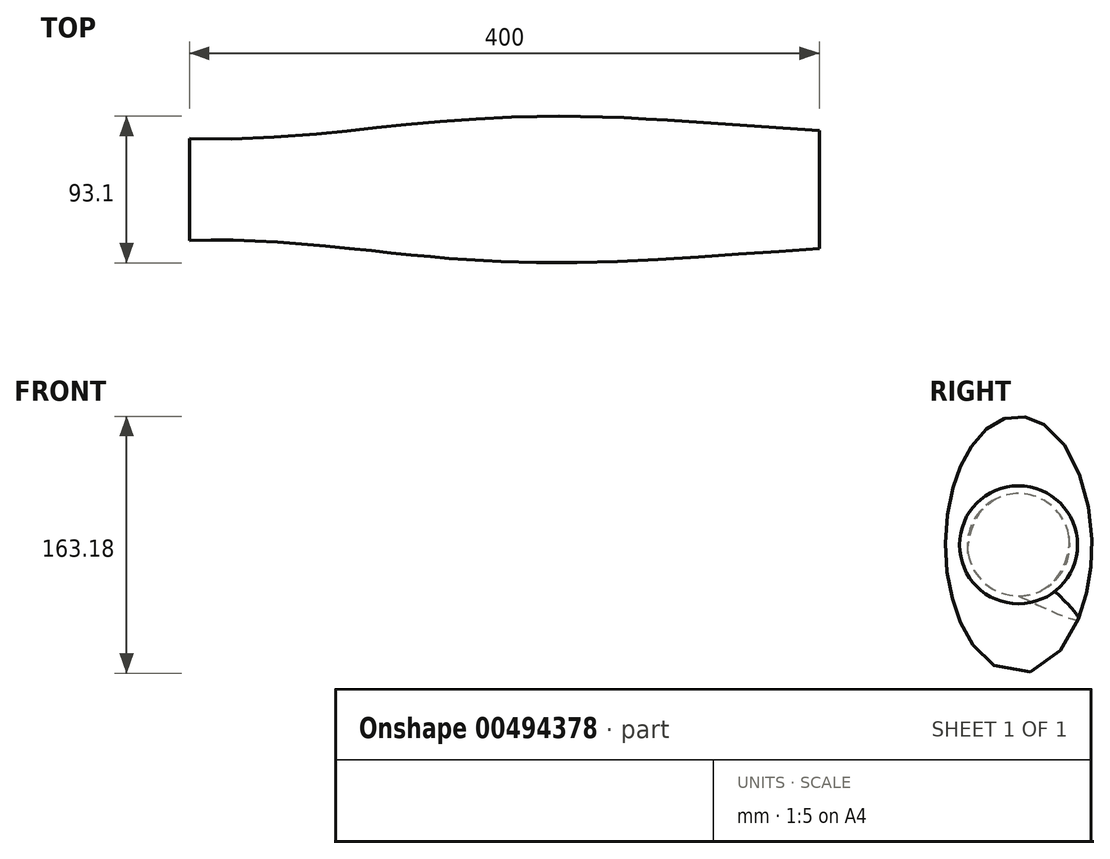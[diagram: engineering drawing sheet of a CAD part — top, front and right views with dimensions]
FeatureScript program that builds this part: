
annotation { "Feature Type Name" : "Feature", "Feature Type Description" : "" }
export const myFeature = defineFeature(function(context is Context, id is Id, definition is map)
    precondition{}
    {
        {
            var Q0;
            Q0=qCreatedBy(makeId("Right.planeOp"),FACE);
            var sketch = newSketch(context, id + "F0", { "sketchPlane" : qUnion([Q0])});
            skEllipse(sketch, "E0", {"center": v(0, 0) * mm, "majorRadius": 45.89 * mm, "minorRadius": 81.4 * mm, "majorAxis": v(1, 0)});
            skSolve(sketch);
        }
        {
            var Q0;
            Q0=qCreatedBy(makeId("Right.planeOp"),FACE);
            cPlane(context, id + "F1", {"entities" : qUnion([Q0]), "cplaneType" : CPlaneType.OFFSET, "offset" : 200 * mm, "width" : 150 * mm, "height" : 150 * mm});
        }
        {
            var Q0;
            Q0=qCreatedBy(id+"F1.planeOp",FACE);
            var sketch = newSketch(context, id + "F2", { "sketchPlane" : qUnion([Q0])});
            skCircle(sketch, "E1", {"center": v(0, 0) * mm, "radius": 37.5 * mm});
            skSolve(sketch);
        }
        {
            var Q0;
            Q0=qCreatedBy(makeId("Right.planeOp"),FACE);
            cPlane(context, id + "F3", {"entities" : qUnion([Q0]), "cplaneType" : CPlaneType.OFFSET, "offset" : 200 * mm, "oppositeDirection" : true, "width" : 150 * mm, "height" : 150 * mm});
        }
        {
            var Q0;
            Q0=qCreatedBy(id+"F3.planeOp",FACE);
            var sketch = newSketch(context, id + "F4", { "sketchPlane" : qUnion([Q0])});
            skCircle(sketch, "E2", {"center": v(0, 0) * mm, "radius": 32.5 * mm});
            skSolve(sketch);
        }
        {
            var Q0;
            Q0 = qSketchRegion(id + "F4", true);
            var Q1;
            Q1 = qSketchRegion(id + "F0", true);
            var Q2;
            Q2=makeQuery(id+"F2.imprint","IMPRINT",FACE,{"disambiguationData":[TD([[makeQuery(id+"F2.imprint","IMPRINT",EDGE,{"derivedFrom":sQuery(id+"F2.wireOp",EDGE,"E1")}),1.0]])]});
            loft(context, id + "F5", {"sheetProfilesArray" : [{ "sheetProfileEntities" : qUnion([Q0]) }, { "sheetProfileEntities" : qUnion([Q1]) }, { "sheetProfileEntities" : qUnion([Q2]) }]});
        }
    });
